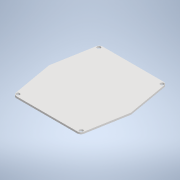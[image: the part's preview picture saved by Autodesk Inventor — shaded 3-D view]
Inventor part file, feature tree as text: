
AUTODESK INVENTOR PART (.ipt)
format: ipt  version: 2021 (Build 250183000, 183)  size: 227,840 bytes
history: native  units: mm
features: reference x27, other x15, extrude x5, sketch x5, loft x2
ambient origin geometry x8: Origin, YZ Plane, XZ Plane, XY Plane, X Axis, Y Axis, Z Axis, Center Point
bodies: Solid1 (feature_tree)
feature tree (54):
  extrude  "Extrusion1"  TaperAngle=0.0deg  [1 undecoded]
  extrude  "Extrusion2"  Depth=95.0mm
  extrude  "Extrusion3"  Depth=95.0mm
  extrude  "Extrusion4"  Depth=2.5mm
  loft  "Loft1"
  extrude  "Extrusion5"  Depth=2.5mm
  sketch  "Sketch1"  dims[d0=5.0mm d1=0.0mm d2=0.0mm d3=0.0mm]
  reference  "Reference1"
  sketch  "Sketch2"  dims[d4=0.0mm d5=0.0mm d6=95.0mm]
  reference  "Reference2"
  reference  "Reference3"
  reference  "Reference4"
  reference  "Reference5"
  sketch  "Sketch3"  dims[d7=120.0mm d8=95.0mm]
  reference  "Reference6"
  reference  "Reference7"
  reference  "Reference8"
  reference  "Reference9"
  sketch  "Sketch4"  dims[d9=120.0mm d10=2.5mm]
  other  "Edges1"
  other  "Edges2"
  other  "Srf1"
  other  "Edges3"
  other  "Edges4"
  sketch  "Sketch5"  dims[d11=2.5mm d12=2.5mm d13=2.5mm d14=50.0mm d15=0.0mm d16=0.0mm d17=90.0deg d18=0.0mm d19=90.0deg d20=0.0mm d21=90.0deg d22=0.0mm d23=90.0deg d24=0.0mm d25=0.0mm]
  reference  "Reference10"
  reference  "Reference11"
  reference  "Reference12"
  reference  "Reference13"
  reference  "Reference14"
  reference  "Reference15"
  reference  "Reference16"
  reference  "Reference17"
  reference  "Reference18"
  reference  "Reference19"
  reference  "Reference20"
  reference  "Reference21"
  reference  "Reference22"
  reference  "Reference23"
  reference  "Reference24"
  reference  "Reference25"
  reference  "Reference26"
  reference  "Reference27"
  loft  "LoftSrf1"
  parser-record x1  (decoder bookkeeping rows leaked as tree rows — omitted from the tree; the rows remain in map.json)
  other  "ilmbt_3d_v1.iam"
  other  "base_:1"
  other  "Arduino Mega ATmega 2560:1"
  other  "Arduino Mega PCB_1"
  other  "GPS_ublox_board:1"
  other  "MPU-9250:1"
  other  "board:1"
  other  "Raspberry Pi:1"
  other  "HCM5883L:1"
note: 1 required parameter value undecoded (feature->parameter linkage not recoverable at this tier; creation-order binding heuristic only, values carry confidence <= 0.55)
note: 1 file-system path scrubbed to <path> (originals preserved in map.json)
